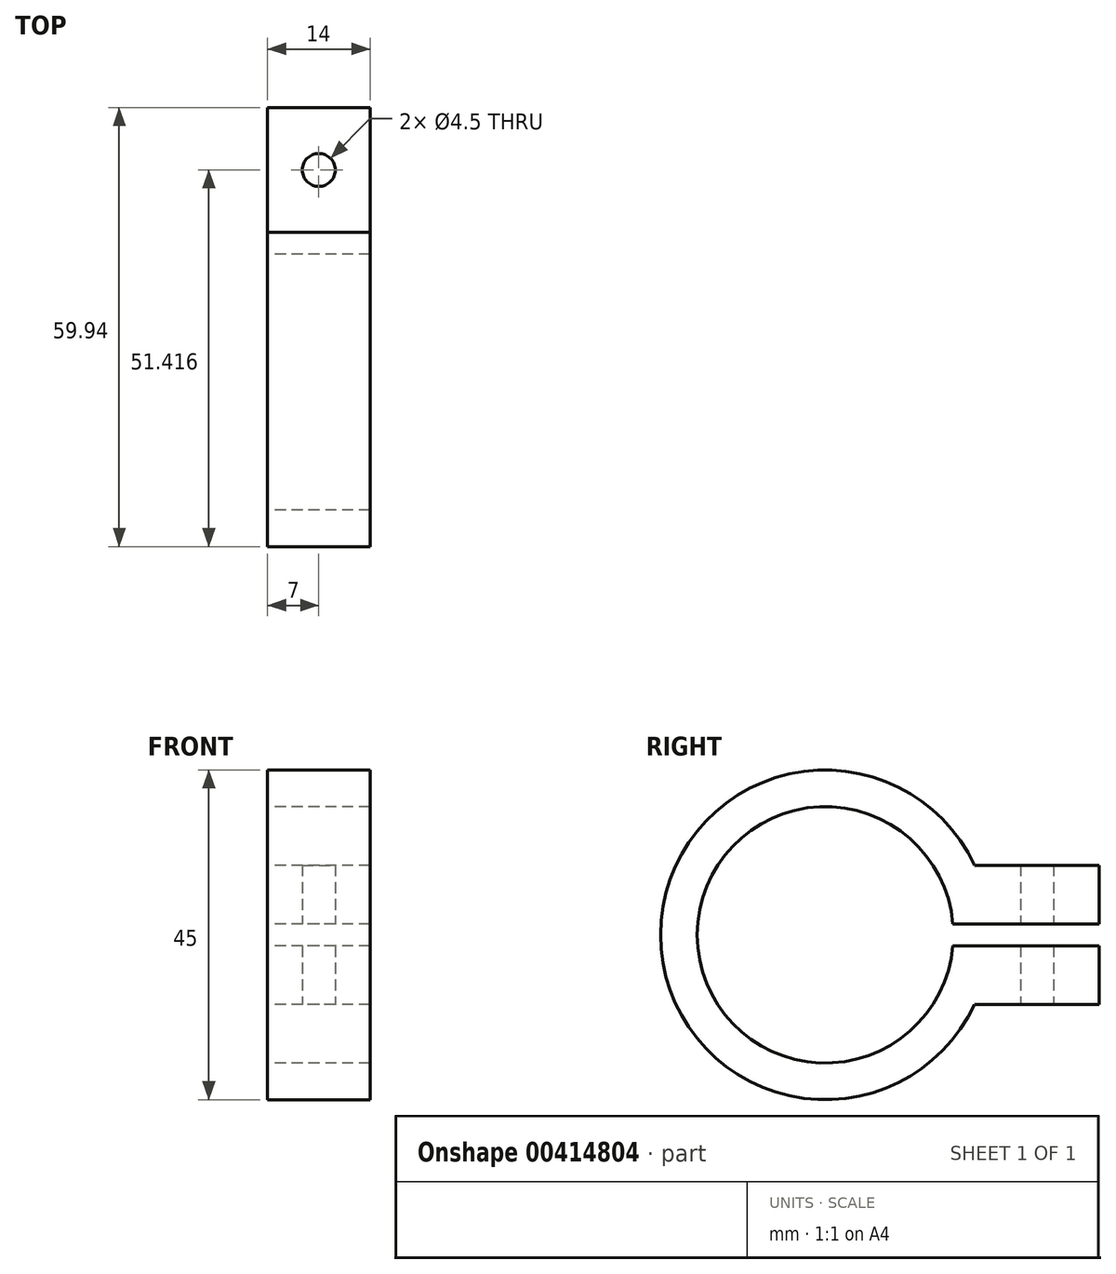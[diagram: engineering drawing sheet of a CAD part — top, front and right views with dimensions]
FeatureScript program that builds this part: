
annotation { "Feature Type Name" : "Feature", "Feature Type Description" : "" }
export const myFeature = defineFeature(function(context is Context, id is Id, definition is map)
    precondition{}
    {
        {
            var Q0;
            Q0=qCreatedBy(makeId("Right.planeOp"),FACE);
            var sketch = newSketch(context, id + "F0", { "sketchPlane" : qUnion([Q0])});
            skArc(sketch, "E0", {"start": v(17.44, 1.5) * mm, "mid": v(-17.5, 0) * mm, "end": v(17.44, -1.5) * mm});
            skArc(sketch, "E1", {"start": v(20.4, 9.5) * mm, "mid": v(-22.5, 0) * mm, "end": v(20.4, -9.5) * mm});
            skLineSegment(sketch, "E2", {"start": v(0, 0) * mm, "end": v(22.5, 0) * mm, "construction": true});
            skLineSegment(sketch, "E3", {"start": v(0, 0) * mm, "end": v(0, 22.5) * mm, "construction": true});
            skLineSegment(sketch, "E4", {"start": v(17.44, 1.5) * mm, "end": v(37.44, 1.5) * mm});
            skLineSegment(sketch, "E5.0", {"start": v(20.4, 9.5) * mm, "end": v(37.44, 9.5) * mm});
            skLineSegment(sketch, "E6", {"start": v(37.44, 9.5) * mm, "end": v(37.44, 1.5) * mm});
            skLineSegment(sketch, "E7.MirrorCS", {"start": v(17.44, -1.5) * mm, "end": v(37.44, -1.5) * mm});
            skLineSegment(sketch, "E8.MirrorCS", {"start": v(37.44, -9.5) * mm, "end": v(37.44, -1.5) * mm});
            skLineSegment(sketch, "E9.MirrorCS", {"start": v(20.4, -9.5) * mm, "end": v(37.44, -9.5) * mm});
            skLineSegment(sketch, "E10.bottom", {"start": v(37.44, -9.5) * mm, "end": v(20.4, -9.5) * mm});
            skLineSegment(sketch, "E10.top", {"start": v(37.44, -34.5) * mm, "end": v(-12.56, -34.5) * mm});
            skLineSegment(sketch, "E10.left", {"start": v(37.44, -9.5) * mm, "end": v(37.44, -34.5) * mm});
            skLineSegment(sketch, "E10.right", {"start": v(-12.56, -18.67) * mm, "end": v(-12.56, -34.5) * mm});
            skSolve(sketch);
        }
        {
            var Q0;
            Q0=makeQuery(id+"F0.imprint","IMPRINT",FACE,{"disambiguationData":[TD([[makeQuery(id+"F0.imprint","IMPRINT",EDGE,{"derivedFrom":sQuery(id+"F0.wireOp",EDGE,"E0")}),-1.0]])]});
            extrude(context, id + "F1", {"entities" : qUnion([Q0]), "depth" : 14 * mm});
        }
        {
            var Q0;
            Q0=makeQuery(id+"F1.opExtrude","SWEPT_FACE",FACE,{"disambiguationData":[OSD([sQuery(id+"F0.wireOp",EDGE,"E5.0")])]});
            var sketch = newSketch(context, id + "F2", { "sketchPlane" : qUnion([Q0])});
            skPoint(sketch, "E11", {"position": v(7, 28.92) * mm});
            skPoint(sketch, "E11.positionSnap0", {"position": v(7, 37.44) * mm});
            skPoint(sketch, "E11.positionSnap1", {"position": v(0, 28.92) * mm});
            skSolve(sketch);
        }
        {
            var Q0;
            Q0=sQuery(id+"F2.wireOp",VERTEX,"E11");
            var Q1;
            Q1=makeQuery(id+"F1.opExtrude","SWEPT_BODY",BODY,{"disambiguationData":[OSD([sQuery(id+"F0.wireOp",EDGE,"E0"),sQuery(id+"F0.wireOp",EDGE,"E1"),sQuery(id+"F0.wireOp",EDGE,"E4"),sQuery(id+"F0.wireOp",EDGE,"E5.0"),sQuery(id+"F0.wireOp",EDGE,"E6"),sQuery(id+"F0.wireOp",EDGE,"E7.MirrorCS"),sQuery(id+"F0.wireOp",EDGE,"E8.MirrorCS"),sQuery(id+"F0.wireOp",EDGE,"E10.bottom")])]});
            hole(context, id + "F3", {"style" : HoleStyle.SIMPLE, "endStyle" : HoleEndStyle.THROUGH, "standardTappedOrClearance" : lookupTablePath({ "standard" : "ISO", "size" : "4.5", "type" : "Drilled" }), "standardBlindInLast" : lookupTablePath({ "standard" : "ISO", "size" : "4.5", "type" : "Drilled" }), "holeDiameter" : 4.5 * mm, "isTappedThrough" : true, "tappedDepth" : 12 * mm, "tapClearance" : 3, "locations" : qUnion([Q0]), "scope" : qUnion([Q1]), "startStyle" : HoleStartStyle.PART});
        }
    });
